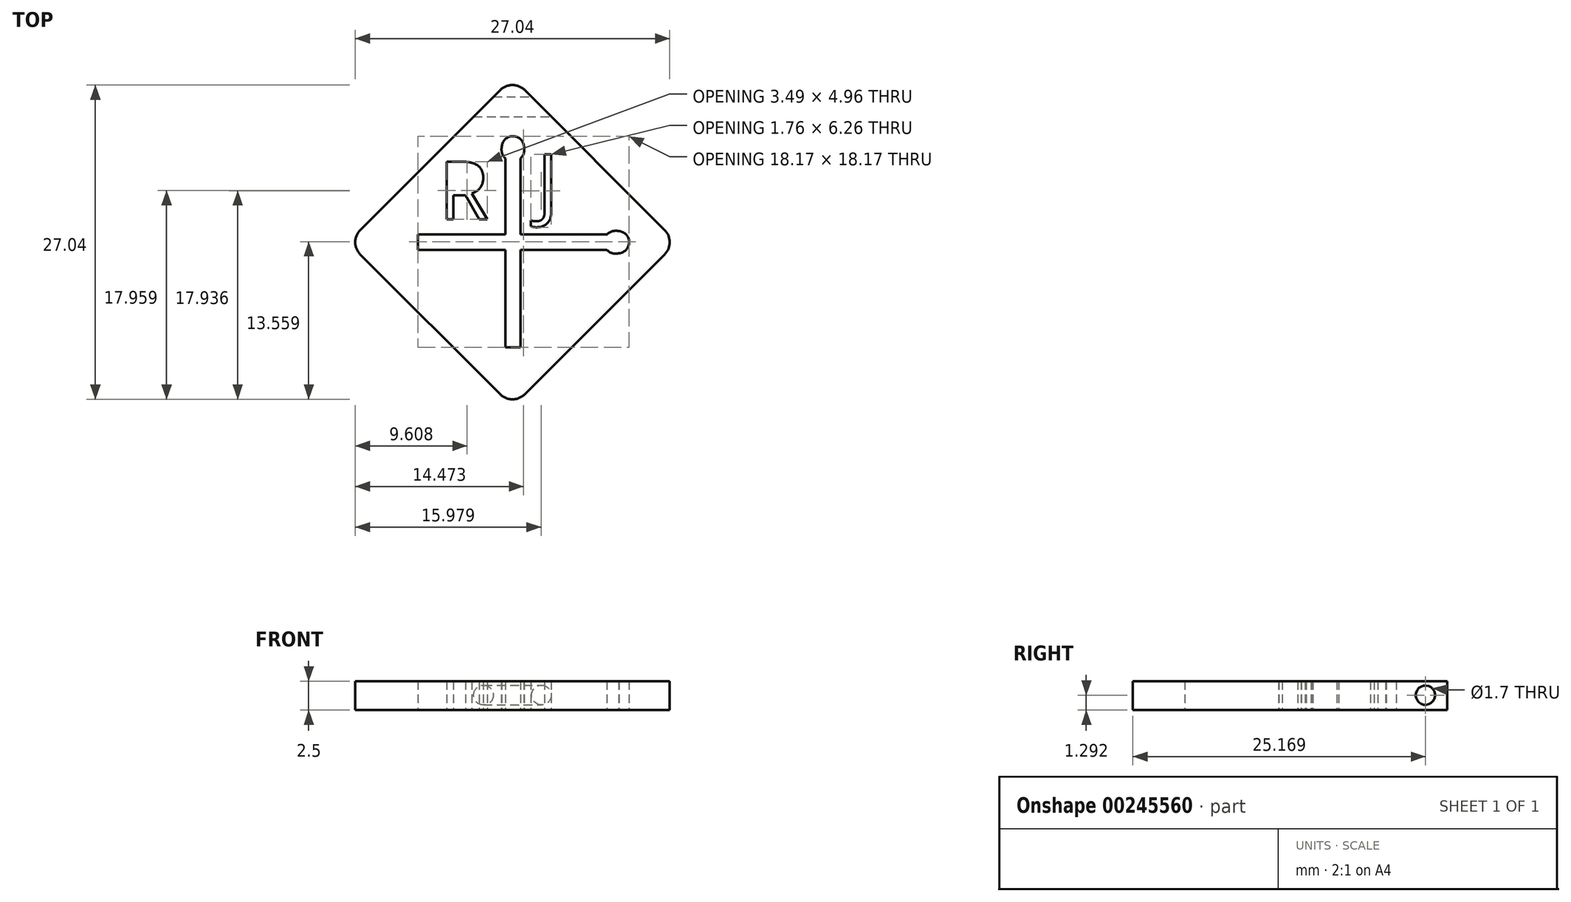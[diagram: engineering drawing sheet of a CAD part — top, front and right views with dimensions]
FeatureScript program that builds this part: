
annotation { "Feature Type Name" : "Feature", "Feature Type Description" : "" }
export const myFeature = defineFeature(function(context is Context, id is Id, definition is map)
    precondition{}
    {
        {
            var Q0;
            Q0=qCreatedBy(makeId("Top.planeOp"),FACE);
            var sketch = newSketch(context, id + "F0", { "sketchPlane" : qUnion([Q0])});
            skLineSegment(sketch, "E0", {"start": v(1.06, -1.06) * mm, "end": v(13.08, -13.08) * mm});
            skLineSegment(sketch, "E1", {"start": v(13.08, -15.2) * mm, "end": v(1.06, -27.22) * mm});
            skLineSegment(sketch, "E2", {"start": v(-1.06, -27.22) * mm, "end": v(-13.08, -15.2) * mm});
            skLineSegment(sketch, "E3", {"start": v(-13.08, -13.08) * mm, "end": v(-1.06, -1.06) * mm});
            skPoint(sketch, "E4.visualSharp", {"position": v(0, 0) * mm});
            skArc(sketch, "E4.filletArc", {"start": v(1.06, -1.06) * mm, "mid": v(0, -0.62) * mm, "end": v(-1.06, -1.06) * mm});
            skPoint(sketch, "E5.visualSharp", {"position": v(-14.14, -14.14) * mm});
            skArc(sketch, "E5.filletArc", {"start": v(-13.08, -13.08) * mm, "mid": v(-13.52, -14.14) * mm, "end": v(-13.08, -15.2) * mm});
            skPoint(sketch, "E6.visualSharp", {"position": v(14.14, -14.14) * mm});
            skArc(sketch, "E6.filletArc", {"start": v(13.08, -15.2) * mm, "mid": v(13.52, -14.14) * mm, "end": v(13.08, -13.08) * mm});
            skPoint(sketch, "E7.visualSharp", {"position": v(0, -28.28) * mm});
            skArc(sketch, "E7.filletArc", {"start": v(-1.06, -27.22) * mm, "mid": v(0, -27.66) * mm, "end": v(1.06, -27.22) * mm});
            skLineSegment(sketch, "E8", {"start": v(0, 0) * mm, "end": v(0, -31.86) * mm, "construction": true});
            skLineSegment(sketch, "E9", {"start": v(-14.14, -14.14) * mm, "end": v(14.14, -14.14) * mm, "construction": true});
            skLineSegment(sketch, "E10", {"start": v(-8.13, -13.48) * mm, "end": v(-8.13, -14.8) * mm});
            skLineSegment(sketch, "E11", {"start": v(-8.13, -14.8) * mm, "end": v(8.13, -14.8) * mm});
            skLineSegment(sketch, "E12", {"start": v(8.13, -13.48) * mm, "end": v(-8.13, -13.48) * mm});
            skLineSegment(sketch, "E13", {"start": v(-8.13, -13.48) * mm, "end": v(0, -13.48) * mm, "construction": true});
            skLineSegment(sketch, "E14", {"start": v(0, -13.48) * mm, "end": v(8.13, -13.48) * mm, "construction": true});
            skArc(sketch, "E15", {"start": v(9.18, -15.1) * mm, "mid": v(10.04, -14.12) * mm, "end": v(9.13, -13.2) * mm});
            skArc(sketch, "E16", {"start": v(9.13, -13.2) * mm, "mid": v(8.6, -13.2) * mm, "end": v(8.13, -13.48) * mm});
            skArc(sketch, "E17", {"start": v(8.13, -14.8) * mm, "mid": v(8.61, -15.1) * mm, "end": v(9.18, -15.1) * mm});
            skLineSegment(sketch, "E18", {"start": v(-0.62, -23.19) * mm, "end": v(0.7, -23.19) * mm});
            skLineSegment(sketch, "E19", {"start": v(0.7, -23.19) * mm, "end": v(0.7, -6.92) * mm});
            skLineSegment(sketch, "E20", {"start": v(-0.62, -6.92) * mm, "end": v(-0.62, -23.19) * mm});
            skLineSegment(sketch, "E21", {"start": v(-0.62, -23.19) * mm, "end": v(-0.62, -15.05) * mm, "construction": true});
            skLineSegment(sketch, "E22", {"start": v(-0.62, -15.05) * mm, "end": v(-0.62, -6.92) * mm, "construction": true});
            skArc(sketch, "E23", {"start": v(0.99, -5.88) * mm, "mid": v(0.02, -5.01) * mm, "end": v(-0.91, -5.92) * mm});
            skArc(sketch, "E24", {"start": v(-0.91, -5.92) * mm, "mid": v(-0.9, -6.46) * mm, "end": v(-0.62, -6.92) * mm});
            skArc(sketch, "E25", {"start": v(0.7, -6.92) * mm, "mid": v(1, -6.44) * mm, "end": v(0.99, -5.88) * mm});
            skText(sketch, "E26", { "text": "R\n", "fontName": "OpenSans-Regular.ttf"});
            skText(sketch, "E27", { "text": "J\n", "fontName": "OpenSans-Regular.ttf"});
            const initialGuessF0  = {"E26": [-0.00634, -0.01218, 1, 0, 0.005], "E27": [0.00212, -0.01155, 1, 0, 0.005]};
            skSetInitialGuess(sketch, initialGuessF0);
            skSolve(sketch);
        }
        {
            var Q0;
            Q0=makeQuery(id+"F0.imprint","IMPRINT",FACE,{"disambiguationData":[TD([[makeQuery(id+"F0.imprint","IMPRINT",EDGE,{"derivedFrom":sQuery(id+"F0.wireOp",EDGE,"E0")}),-1.0]])]});
            extrude(context, id + "F1", {"entities" : qUnion([Q0]), "depth" : 2.5 * mm});
        }
        {
            var Q0;
            Q0=qCreatedBy(makeId("Right.planeOp"),FACE);
            var sketch = newSketch(context, id + "F2", { "sketchPlane" : qUnion([Q0])});
            skCircle(sketch, "E28", {"center": v(-2.5, 1.3) * mm, "radius": 0.85 * mm});
            skSolve(sketch);
        }
        {
            var Q0;
            Q0=qSketchRegion(id+"F2",true);
            extrude(context, id + "F3", {"entities" : qUnion([Q0]), "operationType" : NewBodyOperationType.REMOVE, "endBound" : BoundingType.SYMMETRIC, "oppositeDirection" : true, "depth" : 25 * mm});
        }
    });
